# Revit family: Domotics-DomesticRanges-GEWISS-SYSTEM_COMMAND-PUSH-BUTTON_PULLCORD
name_source: partatom
category: Apparecchi elettrici
revit_build: Autodesk Revit 2016 (Build: 20161004_0715(x64)
units: mm (PartAtom-declared; Revit-internal decimal feet)

## family parameters
Condiviso = Sì
Host = Superficie
Mantenere orientamento annotazione = Sì
Numero OmniClass = 23.80.50.11.14
Punto di calcolo locali = Sì
Quota connettore circolare = Usa diametro
Taglio con vuoti quando caricato = Sì
Tipo di parte = Normale
Titolo OmniClass = Switches

## types (2) — shared parameters
Button key = With pull-cord
Carico apparente = 0 VA
Catalogue = DOMOTICS
Catalogue Range = SYSTEM - DOMESTIC RANGE
Description. = Push-button (2P)
Description: = 2P NO - 10A
Electrocod = 0130
IDF = 98acc4a6-a4e7-491b-a0af-8e79f6c445f9
IDT = fee25026-a03e-4863-bd7c-ede036428934
Immagine tipo = gw21518.jpg
N. poli = 1
No. SYSTEM modules = 1
Produttore = GEWISS S.p.A.
Prospetto di default = 1219 mm
Pulsante = GEWISS NERO
SEO = Push button
Simbolo = SIMBOLO PULSANTI : PULSTIRANTE
Technical sheet = https://www.gewiss.com
Type = With pull-cord
URL = https://www.gewiss.com
Version file RFA = 19.4
Volt = 230 V
Voltage = 250 V ac
Voltage: = 250 V ac

## per-type parameters (varying)
| type | Colour | Descrizione | EAN code | Modello |
| GW20518 - Push-button-2P NO 10A pull-cord white | White | PUSH-BUTTON-2P NO 10A PULL-CORD SY/WT | 8011564077362 | GW20518 |
| GW21518 - Push-button-2P NO 10A pull-cord black | Black | PUSH-BUTTON-2P NA 10A PULL-CORD SY/BK | 8011564128187 | GW21518 |

## geometry (parser evidence)
native form markers: Sweep x1
no freeform markers — native parametric forms only
